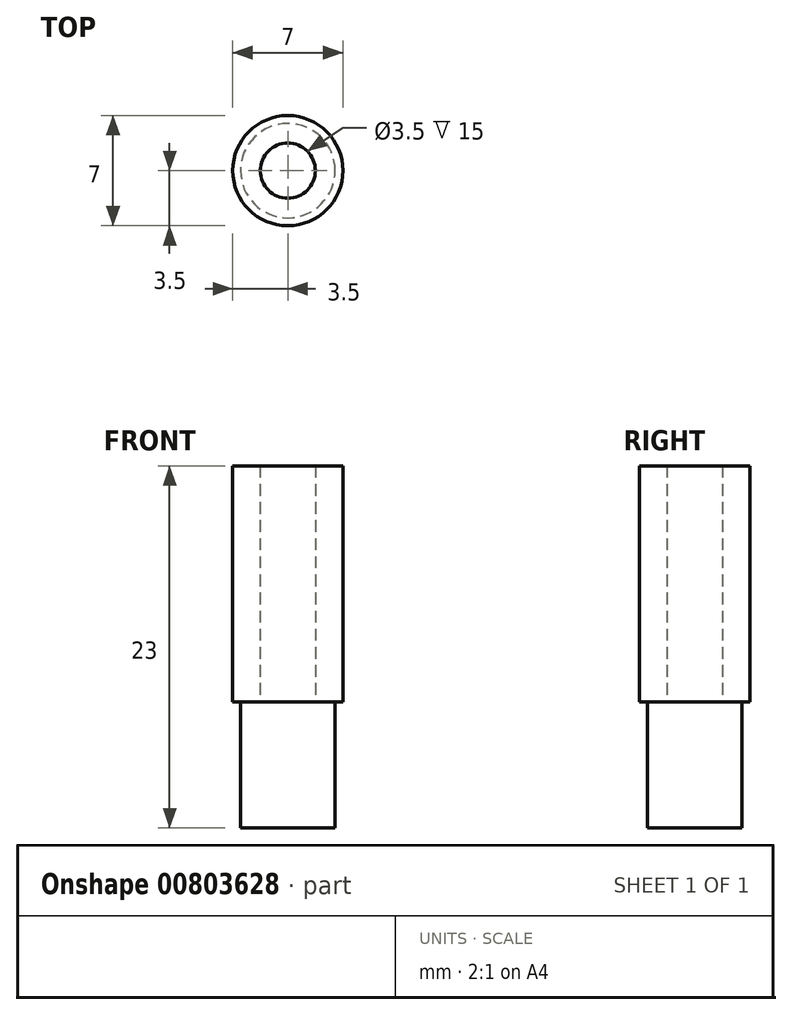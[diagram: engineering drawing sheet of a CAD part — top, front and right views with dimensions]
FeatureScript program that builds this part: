
annotation { "Feature Type Name" : "Feature", "Feature Type Description" : "" }
export const myFeature = defineFeature(function(context is Context, id is Id, definition is map)
    precondition{}
    {
        {
            var Q0;
            Q0=qCreatedBy(makeId("Top.planeOp"),FACE);
            var sketch = newSketch(context, id + "F0", { "sketchPlane" : qUnion([Q0])});
            skCircle(sketch, "E0", {"center": v(0, 0) * mm, "radius": 3 * mm});
            skSolve(sketch);
        }
        {
            var Q0;
            Q0 = qSketchRegion(id + "F0", true);
            extrude(context, id + "F1", {"entities" : qUnion([Q0]), "depth" : 8 * mm, "offsetDistance" : 25 * mm});
        }
        {
            var Q0;
            Q0=makeQuery(id+"F1.opExtrude","CAP_FACE",FACE,{"disambiguationData":[OSD([sQuery(id+"F0.wireOp",EDGE,"E0")])],"isStart":false});
            var sketch = newSketch(context, id + "F2", { "sketchPlane" : qUnion([Q0])});
            skCircle(sketch, "E1", {"center": v(0, 0) * mm, "radius": 3.5 * mm});
            skCircle(sketch, "E2", {"center": v(0, 0) * mm, "radius": 1.75 * mm});
            skSolve(sketch);
        }
        {
            var Q0;
            Q0=makeQuery(id+"F2.imprint","IMPRINT",FACE,{"disambiguationData":[TD([[makeQuery(id+"F2.imprint","IMPRINT",EDGE,{"derivedFrom":sQuery(id+"F2.wireOp",EDGE,"E2")}),-1.0]])]});
            var Q1;
            Q1=makeQuery(id+"F2.imprint","IMPRINT",FACE,{"disambiguationData":[TD([[makeQuery(id+"F2.imprint","IMPRINT",EDGE,{"derivedFrom":sQuery(id+"F2.wireOp",EDGE,"E1")}),1.0]])]});
            extrude(context, id + "F3", {"entities" : qUnion([Q0, Q1]), "operationType" : NewBodyOperationType.ADD, "depth" : 15 * mm, "offsetDistance" : 25 * mm});
        }
    });
